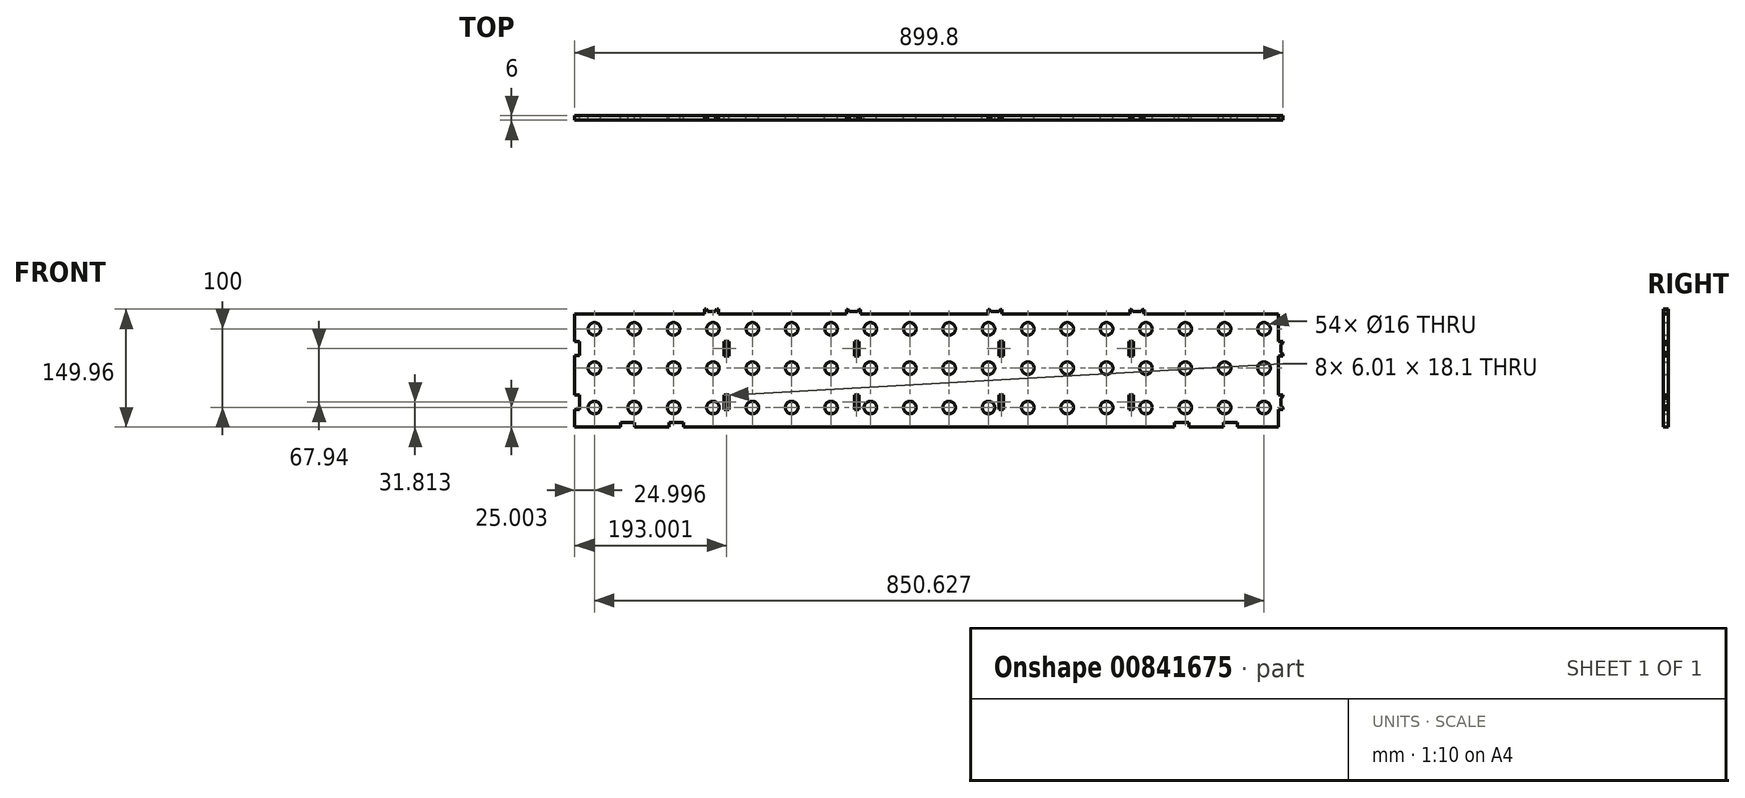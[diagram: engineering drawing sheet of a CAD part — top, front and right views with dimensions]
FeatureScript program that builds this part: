
annotation { "Feature Type Name" : "Feature", "Feature Type Description" : "" }
export const myFeature = defineFeature(function(context is Context, id is Id, definition is map)
    precondition{}
    {
        {
            var Q0;
            Q0=qCreatedBy(makeId("Front.planeOp"),FACE);
            var sketch = newSketch(context, id + "F0", { "sketchPlane" : qUnion([Q0])});
            skLineSegment(sketch, "E0.bottom", {"start": v(-31.25, -172.7) * mm, "end": v(133.75, -172.7) * mm});
            skLineSegment(sketch, "E0.top", {"start": v(-31.25, -316.7) * mm, "end": v(26.75, -316.7) * mm});
            skPoint(sketch, "E1.orphan", {"position": v(-25.02, 5.3) * mm});
            skLineSegment(sketch, "E2", {"start": v(-31.25, -316.7) * mm, "end": v(-31.25, -293.94) * mm});
            skLineSegment(sketch, "E3", {"start": v(862.75, -172.7) * mm, "end": v(862.75, -207.9) * mm});
            skLineSegment(sketch, "E4", {"start": v(133.75, -172.7) * mm, "end": v(133.75, -166.74) * mm});
            skLineSegment(sketch, "E5", {"start": v(133.75, -166.74) * mm, "end": v(135.75, -166.74) * mm});
            skLineSegment(sketch, "E6", {"start": v(135.75, -166.74) * mm, "end": v(137.75, -169.7) * mm});
            skLineSegment(sketch, "E7", {"start": v(137.75, -169.7) * mm, "end": v(147.75, -169.7) * mm});
            skLineSegment(sketch, "E8", {"start": v(147.75, -169.7) * mm, "end": v(149.75, -166.74) * mm});
            skLineSegment(sketch, "E9", {"start": v(149.75, -166.74) * mm, "end": v(151.75, -166.74) * mm});
            skLineSegment(sketch, "E10", {"start": v(151.75, -166.74) * mm, "end": v(151.75, -172.7) * mm});
            skLineSegment(sketch, "E11.trimOffspring", {"start": v(151.75, -172.7) * mm, "end": v(313.75, -172.7) * mm});
            skLineSegment(sketch, "E12.trimOffspring", {"start": v(331.75, -172.7) * mm, "end": v(493.75, -172.7) * mm});
            skLineSegment(sketch, "E13", {"start": v(493.75, -172.7) * mm, "end": v(493.75, -166.9) * mm});
            skLineSegment(sketch, "E14", {"start": v(493.75, -166.9) * mm, "end": v(495.75, -166.9) * mm});
            skLineSegment(sketch, "E15", {"start": v(495.75, -166.9) * mm, "end": v(497.75, -169.7) * mm});
            skLineSegment(sketch, "E16", {"start": v(497.75, -169.7) * mm, "end": v(507.75, -169.7) * mm});
            skLineSegment(sketch, "E17", {"start": v(507.75, -169.7) * mm, "end": v(509.75, -166.9) * mm});
            skLineSegment(sketch, "E18", {"start": v(509.75, -166.9) * mm, "end": v(511.75, -166.9) * mm});
            skLineSegment(sketch, "E19", {"start": v(511.75, -166.9) * mm, "end": v(511.75, -172.7) * mm});
            skLineSegment(sketch, "E20.trimOffspring", {"start": v(511.75, -172.7) * mm, "end": v(673.75, -172.7) * mm});
            skLineSegment(sketch, "E21", {"start": v(673.75, -172.7) * mm, "end": v(673.75, -166.9) * mm});
            skLineSegment(sketch, "E22", {"start": v(673.75, -166.9) * mm, "end": v(675.75, -166.9) * mm});
            skLineSegment(sketch, "E23", {"start": v(675.75, -166.9) * mm, "end": v(677.75, -169.7) * mm});
            skLineSegment(sketch, "E24", {"start": v(677.75, -169.7) * mm, "end": v(687.75, -169.7) * mm});
            skLineSegment(sketch, "E25", {"start": v(687.75, -169.7) * mm, "end": v(689.75, -166.9) * mm});
            skLineSegment(sketch, "E26", {"start": v(689.75, -166.9) * mm, "end": v(691.75, -166.9) * mm});
            skLineSegment(sketch, "E27", {"start": v(691.75, -166.9) * mm, "end": v(691.75, -172.7) * mm});
            skLineSegment(sketch, "E28.trimOffspring", {"start": v(691.75, -172.7) * mm, "end": v(862.75, -172.7) * mm});
            skLineSegment(sketch, "E29", {"start": v(-31.25, -191.7) * mm, "end": v(862.75, -191.7) * mm, "construction": true});
            skCircle(sketch, "E30", {"center": v(-6.25, -191.7) * mm, "radius": 8 * mm});
            skCircle(sketch, "E31", {"center": v(44.37, -191.7) * mm, "radius": 8 * mm});
            skCircle(sketch, "E32", {"center": v(94.37, -191.7) * mm, "radius": 8 * mm});
            skCircle(sketch, "E33", {"center": v(144.37, -191.7) * mm, "radius": 8 * mm});
            skCircle(sketch, "E34", {"center": v(194.37, -191.7) * mm, "radius": 8 * mm});
            skCircle(sketch, "E35", {"center": v(244.37, -191.7) * mm, "radius": 8 * mm});
            skCircle(sketch, "E36", {"center": v(294.37, -191.7) * mm, "radius": 8 * mm});
            skCircle(sketch, "E37", {"center": v(344.37, -191.7) * mm, "radius": 8 * mm});
            skCircle(sketch, "E38", {"center": v(394.37, -191.7) * mm, "radius": 8 * mm});
            skCircle(sketch, "E39", {"center": v(444.37, -191.7) * mm, "radius": 8 * mm});
            skCircle(sketch, "E40", {"center": v(494.37, -191.7) * mm, "radius": 8 * mm});
            skCircle(sketch, "E41", {"center": v(544.37, -191.7) * mm, "radius": 8 * mm});
            skCircle(sketch, "E42", {"center": v(594.37, -191.7) * mm, "radius": 8 * mm});
            skCircle(sketch, "E43", {"center": v(644.37, -191.7) * mm, "radius": 8 * mm});
            skCircle(sketch, "E44", {"center": v(744.37, -191.7) * mm, "radius": 8 * mm});
            skCircle(sketch, "E45", {"center": v(694.37, -191.7) * mm, "radius": 8 * mm});
            skCircle(sketch, "E46", {"center": v(794.37, -191.7) * mm, "radius": 8 * mm});
            skCircle(sketch, "E47", {"center": v(844.37, -191.7) * mm, "radius": 8 * mm});
            skLineSegment(sketch, "E48", {"start": v(-6.25, -191.7) * mm, "end": v(-6.25, -355.87) * mm, "construction": true});
            skLineSegment(sketch, "E49", {"start": v(-31.25, -241.7) * mm, "end": v(862.75, -241.7) * mm, "construction": true});
            skCircle(sketch, "E50", {"center": v(-6.25, -241.7) * mm, "radius": 8 * mm});
            skCircle(sketch, "E51", {"center": v(44.37, -241.7) * mm, "radius": 8 * mm});
            skCircle(sketch, "E52", {"center": v(94.37, -241.7) * mm, "radius": 8 * mm});
            skCircle(sketch, "E53", {"center": v(144.37, -241.7) * mm, "radius": 8 * mm});
            skCircle(sketch, "E54", {"center": v(194.37, -241.7) * mm, "radius": 8 * mm});
            skCircle(sketch, "E55", {"center": v(244.37, -241.7) * mm, "radius": 8 * mm});
            skCircle(sketch, "E56", {"center": v(294.37, -241.7) * mm, "radius": 8 * mm});
            skCircle(sketch, "E57", {"center": v(344.37, -241.7) * mm, "radius": 8 * mm});
            skCircle(sketch, "E58", {"center": v(394.37, -241.7) * mm, "radius": 8 * mm});
            skCircle(sketch, "E59", {"center": v(444.37, -241.7) * mm, "radius": 8 * mm});
            skCircle(sketch, "E60", {"center": v(494.37, -241.7) * mm, "radius": 8 * mm});
            skCircle(sketch, "E61", {"center": v(544.37, -241.7) * mm, "radius": 8 * mm});
            skCircle(sketch, "E62", {"center": v(594.37, -241.7) * mm, "radius": 8 * mm});
            skCircle(sketch, "E63", {"center": v(644.37, -241.7) * mm, "radius": 8 * mm});
            skCircle(sketch, "E64", {"center": v(744.37, -241.7) * mm, "radius": 8 * mm});
            skCircle(sketch, "E65", {"center": v(694.37, -241.7) * mm, "radius": 8 * mm});
            skCircle(sketch, "E66", {"center": v(794.37, -241.7) * mm, "radius": 8 * mm});
            skCircle(sketch, "E67", {"center": v(844.37, -241.7) * mm, "radius": 8 * mm});
            skLineSegment(sketch, "E68", {"start": v(-31.25, -291.7) * mm, "end": v(862.75, -291.7) * mm, "construction": true});
            skCircle(sketch, "E69", {"center": v(-6.25, -291.7) * mm, "radius": 8 * mm});
            skCircle(sketch, "E70", {"center": v(44.37, -291.7) * mm, "radius": 8 * mm});
            skCircle(sketch, "E71", {"center": v(94.37, -291.7) * mm, "radius": 8 * mm});
            skCircle(sketch, "E72", {"center": v(144.37, -291.7) * mm, "radius": 8 * mm});
            skCircle(sketch, "E73", {"center": v(194.37, -291.7) * mm, "radius": 8 * mm});
            skCircle(sketch, "E74", {"center": v(244.37, -291.7) * mm, "radius": 8 * mm});
            skCircle(sketch, "E75", {"center": v(294.37, -291.7) * mm, "radius": 8 * mm});
            skCircle(sketch, "E76", {"center": v(344.37, -291.7) * mm, "radius": 8 * mm});
            skCircle(sketch, "E77", {"center": v(394.37, -291.7) * mm, "radius": 8 * mm});
            skCircle(sketch, "E78", {"center": v(444.37, -291.7) * mm, "radius": 8 * mm});
            skCircle(sketch, "E79", {"center": v(494.37, -291.7) * mm, "radius": 8 * mm});
            skCircle(sketch, "E80", {"center": v(544.37, -291.7) * mm, "radius": 8 * mm});
            skCircle(sketch, "E81", {"center": v(594.37, -291.7) * mm, "radius": 8 * mm});
            skCircle(sketch, "E82", {"center": v(644.37, -291.7) * mm, "radius": 8 * mm});
            skCircle(sketch, "E83", {"center": v(744.37, -291.7) * mm, "radius": 8 * mm});
            skCircle(sketch, "E84", {"center": v(694.37, -291.7) * mm, "radius": 8 * mm});
            skCircle(sketch, "E85", {"center": v(794.37, -291.7) * mm, "radius": 8 * mm});
            skCircle(sketch, "E86", {"center": v(844.37, -291.7) * mm, "radius": 8 * mm});
            skLineSegment(sketch, "E87", {"start": v(-31.25, -207.74) * mm, "end": v(-25.24, -207.74) * mm});
            skLineSegment(sketch, "E88", {"start": v(-25.24, -207.74) * mm, "end": v(-25.24, -225.84) * mm});
            skLineSegment(sketch, "E89", {"start": v(-25.24, -225.84) * mm, "end": v(-31.25, -225.84) * mm});
            skLineSegment(sketch, "E90", {"start": v(-31.25, -275.84) * mm, "end": v(-25.24, -275.84) * mm});
            skLineSegment(sketch, "E91", {"start": v(-25.24, -275.84) * mm, "end": v(-25.24, -293.94) * mm});
            skLineSegment(sketch, "E92", {"start": v(-25.24, -293.94) * mm, "end": v(-31.25, -293.94) * mm});
            skLineSegment(sketch, "E93.trimOffspring", {"start": v(-31.25, -207.74) * mm, "end": v(-31.25, -172.7) * mm});
            skLineSegment(sketch, "E94.trimOffspring", {"start": v(-31.25, -275.84) * mm, "end": v(-31.25, -225.84) * mm});
            skLineSegment(sketch, "E95", {"start": v(862.75, -207.9) * mm, "end": v(868.55, -207.9) * mm});
            skLineSegment(sketch, "E96", {"start": v(868.55, -207.9) * mm, "end": v(868.55, -209.9) * mm});
            skLineSegment(sketch, "E97", {"start": v(868.55, -209.9) * mm, "end": v(865.75, -211.9) * mm});
            skLineSegment(sketch, "E98", {"start": v(865.75, -211.9) * mm, "end": v(865.75, -221.9) * mm});
            skLineSegment(sketch, "E99", {"start": v(865.75, -221.9) * mm, "end": v(868.55, -223.9) * mm});
            skLineSegment(sketch, "E100", {"start": v(868.55, -223.9) * mm, "end": v(868.55, -225.9) * mm});
            skLineSegment(sketch, "E101", {"start": v(868.55, -225.9) * mm, "end": v(862.75, -225.9) * mm});
            skLineSegment(sketch, "E102", {"start": v(862.75, -275.93) * mm, "end": v(868.55, -275.93) * mm});
            skLineSegment(sketch, "E103", {"start": v(868.55, -275.93) * mm, "end": v(868.55, -277.93) * mm});
            skLineSegment(sketch, "E104", {"start": v(868.55, -277.93) * mm, "end": v(865.75, -279.93) * mm});
            skLineSegment(sketch, "E105", {"start": v(865.75, -279.93) * mm, "end": v(865.75, -289.93) * mm});
            skLineSegment(sketch, "E106", {"start": v(865.75, -289.93) * mm, "end": v(868.55, -291.93) * mm});
            skLineSegment(sketch, "E107", {"start": v(868.55, -291.93) * mm, "end": v(868.55, -293.93) * mm});
            skLineSegment(sketch, "E108", {"start": v(868.55, -293.93) * mm, "end": v(862.75, -293.93) * mm});
            skLineSegment(sketch, "E109.trimOffspring", {"start": v(862.75, -225.9) * mm, "end": v(862.75, -275.93) * mm});
            skLineSegment(sketch, "E110.trimOffspring", {"start": v(862.75, -293.93) * mm, "end": v(862.75, -316.7) * mm});
            skLineSegment(sketch, "E111", {"start": v(313.75, -172.7) * mm, "end": v(313.75, -166.9) * mm});
            skLineSegment(sketch, "E112", {"start": v(313.75, -166.9) * mm, "end": v(315.75, -166.9) * mm});
            skLineSegment(sketch, "E113", {"start": v(315.75, -166.9) * mm, "end": v(317.75, -169.7) * mm});
            skLineSegment(sketch, "E114", {"start": v(317.75, -169.7) * mm, "end": v(327.75, -169.7) * mm});
            skLineSegment(sketch, "E115", {"start": v(327.75, -169.7) * mm, "end": v(329.75, -166.9) * mm});
            skLineSegment(sketch, "E116", {"start": v(329.75, -166.9) * mm, "end": v(331.75, -166.9) * mm});
            skLineSegment(sketch, "E117", {"start": v(331.75, -166.9) * mm, "end": v(331.75, -172.7) * mm});
            skLineSegment(sketch, "E118.bottom", {"start": v(158.75, -207.9) * mm, "end": v(164.76, -207.9) * mm});
            skLineSegment(sketch, "E118.top", {"start": v(158.75, -226) * mm, "end": v(164.76, -226) * mm});
            skLineSegment(sketch, "E118.left", {"start": v(158.75, -207.9) * mm, "end": v(158.75, -226) * mm});
            skLineSegment(sketch, "E118.right", {"start": v(164.76, -207.9) * mm, "end": v(164.76, -226) * mm});
            skLineSegment(sketch, "E119.bottom", {"start": v(158.75, -275.84) * mm, "end": v(164.76, -275.84) * mm});
            skLineSegment(sketch, "E119.top", {"start": v(158.75, -293.94) * mm, "end": v(164.76, -293.94) * mm});
            skLineSegment(sketch, "E119.left", {"start": v(158.75, -275.84) * mm, "end": v(158.75, -293.94) * mm});
            skLineSegment(sketch, "E119.right", {"start": v(164.76, -275.84) * mm, "end": v(164.76, -293.94) * mm});
            skLineSegment(sketch, "E120.bottom", {"start": v(323.95, -226) * mm, "end": v(329.96, -226) * mm});
            skLineSegment(sketch, "E120.top", {"start": v(323.95, -207.9) * mm, "end": v(329.96, -207.9) * mm});
            skLineSegment(sketch, "E120.left", {"start": v(323.95, -226) * mm, "end": v(323.95, -207.9) * mm});
            skLineSegment(sketch, "E120.right", {"start": v(329.96, -226) * mm, "end": v(329.96, -207.9) * mm});
            skLineSegment(sketch, "E121.bottom", {"start": v(329.96, -293.94) * mm, "end": v(323.95, -293.94) * mm});
            skLineSegment(sketch, "E121.top", {"start": v(329.96, -275.84) * mm, "end": v(323.95, -275.84) * mm});
            skLineSegment(sketch, "E121.left", {"start": v(329.96, -293.94) * mm, "end": v(329.96, -275.84) * mm});
            skLineSegment(sketch, "E121.right", {"start": v(323.95, -293.94) * mm, "end": v(323.95, -275.84) * mm});
            skLineSegment(sketch, "E122.bottom", {"start": v(507.54, -207.9) * mm, "end": v(513.55, -207.9) * mm});
            skLineSegment(sketch, "E122.top", {"start": v(507.54, -226) * mm, "end": v(513.55, -226) * mm});
            skLineSegment(sketch, "E122.left", {"start": v(507.54, -207.9) * mm, "end": v(507.54, -226) * mm});
            skLineSegment(sketch, "E122.right", {"start": v(513.55, -207.9) * mm, "end": v(513.55, -226) * mm});
            skLineSegment(sketch, "E123.bottom", {"start": v(513.55, -293.94) * mm, "end": v(507.54, -293.94) * mm});
            skLineSegment(sketch, "E123.top", {"start": v(513.55, -275.84) * mm, "end": v(507.54, -275.84) * mm});
            skLineSegment(sketch, "E123.left", {"start": v(513.55, -293.94) * mm, "end": v(513.55, -275.84) * mm});
            skLineSegment(sketch, "E123.right", {"start": v(507.54, -293.94) * mm, "end": v(507.54, -275.84) * mm});
            skLineSegment(sketch, "E124.bottom", {"start": v(672.74, -207.9) * mm, "end": v(678.75, -207.9) * mm});
            skLineSegment(sketch, "E124.top", {"start": v(672.74, -226) * mm, "end": v(678.75, -226) * mm});
            skLineSegment(sketch, "E124.left", {"start": v(672.74, -207.9) * mm, "end": v(672.74, -226) * mm});
            skLineSegment(sketch, "E124.right", {"start": v(678.75, -207.9) * mm, "end": v(678.75, -226) * mm});
            skLineSegment(sketch, "E125.bottom", {"start": v(672.74, -275.84) * mm, "end": v(678.75, -275.84) * mm});
            skLineSegment(sketch, "E125.top", {"start": v(672.74, -293.94) * mm, "end": v(678.75, -293.94) * mm});
            skLineSegment(sketch, "E125.left", {"start": v(672.74, -275.84) * mm, "end": v(672.74, -293.94) * mm});
            skLineSegment(sketch, "E125.right", {"start": v(678.75, -275.84) * mm, "end": v(678.75, -293.94) * mm});
            skLineSegment(sketch, "E126", {"start": v(26.75, -316.7) * mm, "end": v(26.75, -310.69) * mm});
            skLineSegment(sketch, "E127", {"start": v(26.75, -310.69) * mm, "end": v(44.85, -310.69) * mm});
            skLineSegment(sketch, "E128", {"start": v(44.85, -310.69) * mm, "end": v(44.85, -316.7) * mm});
            skLineSegment(sketch, "E129", {"start": v(88.75, -316.7) * mm, "end": v(88.75, -310.69) * mm});
            skLineSegment(sketch, "E130", {"start": v(88.75, -310.69) * mm, "end": v(106.85, -310.69) * mm});
            skLineSegment(sketch, "E131", {"start": v(106.85, -310.69) * mm, "end": v(106.85, -316.7) * mm});
            skLineSegment(sketch, "E132.trimOffspring", {"start": v(44.85, -316.7) * mm, "end": v(88.75, -316.7) * mm});
            skLineSegment(sketch, "E133.trimOffspring", {"start": v(106.85, -316.7) * mm, "end": v(730.65, -316.7) * mm});
            skLineSegment(sketch, "E134", {"start": v(810.75, -316.7) * mm, "end": v(810.75, -310.69) * mm});
            skLineSegment(sketch, "E135", {"start": v(810.75, -310.69) * mm, "end": v(792.65, -310.69) * mm});
            skLineSegment(sketch, "E136", {"start": v(792.65, -310.69) * mm, "end": v(792.65, -316.7) * mm});
            skLineSegment(sketch, "E137", {"start": v(748.75, -316.7) * mm, "end": v(748.75, -310.69) * mm});
            skLineSegment(sketch, "E138", {"start": v(748.75, -310.69) * mm, "end": v(730.65, -310.69) * mm});
            skLineSegment(sketch, "E139", {"start": v(730.65, -310.69) * mm, "end": v(730.65, -316.7) * mm});
            skLineSegment(sketch, "E140.trimOffspring", {"start": v(748.75, -316.7) * mm, "end": v(792.65, -316.7) * mm});
            skLineSegment(sketch, "E141.trimOffspring", {"start": v(810.75, -316.7) * mm, "end": v(862.75, -316.7) * mm});
            skSolve(sketch);
        }
        {
            var Q0;
            Q0=makeQuery(id+"F0.imprint","IMPRINT",FACE,{"disambiguationData":[TD([[makeQuery(id+"F0.imprint","IMPRINT",EDGE,{"derivedFrom":sQuery(id+"F0.wireOp",EDGE,"E0.bottom")}),-1.0]])]});
            extrude(context, id + "F1", {"entities" : qUnion([Q0]), "depth" : 6 * mm, "offsetDistance" : 25 * mm});
        }
    });
